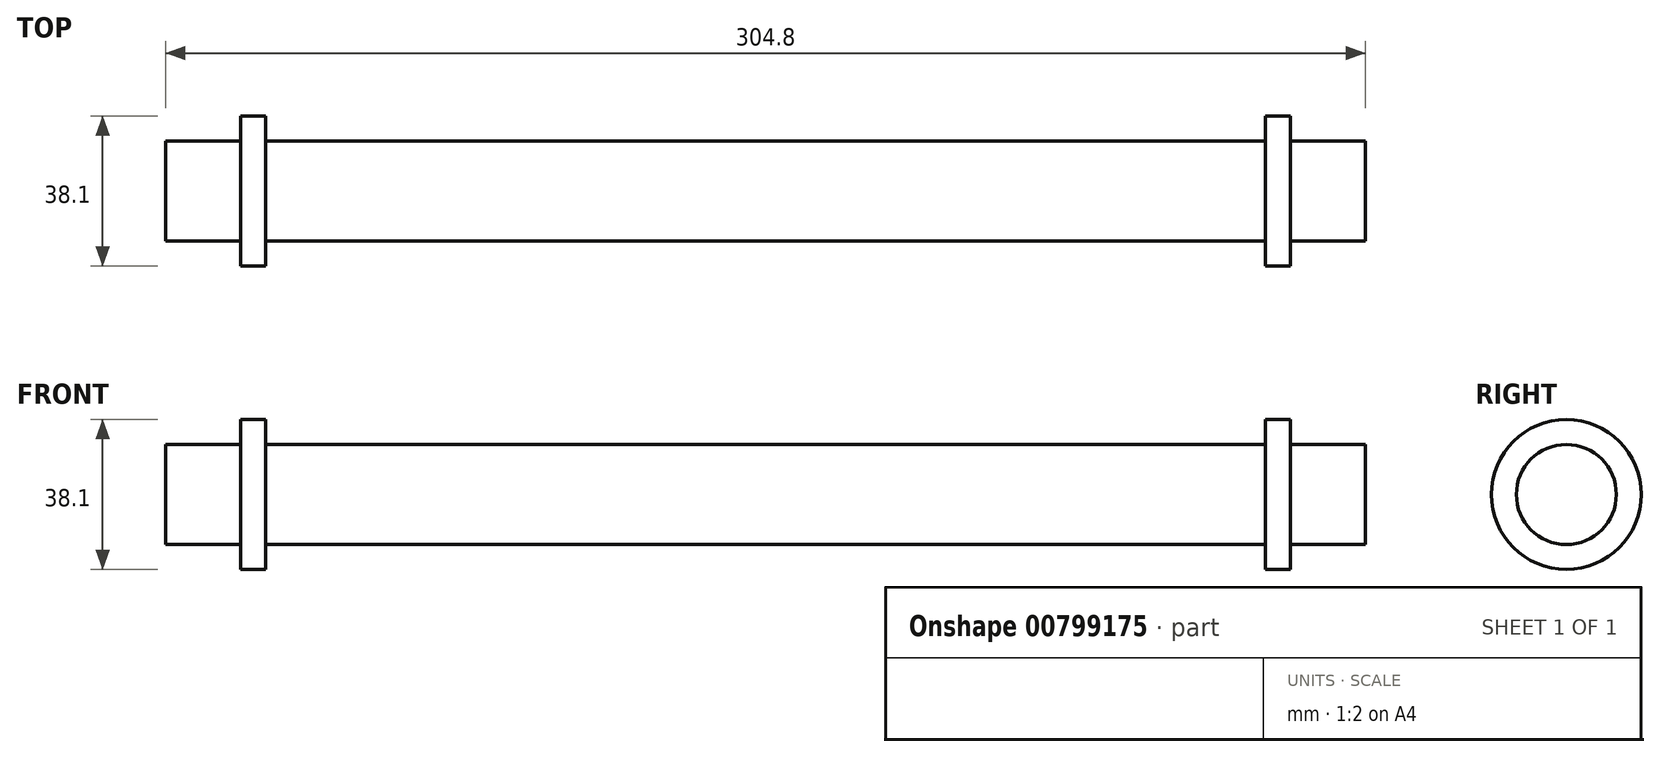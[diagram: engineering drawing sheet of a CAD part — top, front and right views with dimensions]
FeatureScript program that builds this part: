
annotation { "Feature Type Name" : "Feature", "Feature Type Description" : "" }
export const myFeature = defineFeature(function(context is Context, id is Id, definition is map)
    precondition{}
    {
        {
            var Q0;
            Q0=qCreatedBy(makeId("Right.planeOp"),FACE);
            var sketch = newSketch(context, id + "F0", { "sketchPlane" : qUnion([Q0])});
            skCircle(sketch, "E0", {"center": v(0, 0) * mm, "radius": 12.7 * mm});
            skSolve(sketch);
        }
        {
            var Q0;
            Q0=qSketchRegion(id+"F0",true);
            extrude(context, id + "F1", {"entities" : qUnion([Q0]), "endBound" : BoundingType.SYMMETRIC, "depth" : 304.8 * mm});
        }
        {
            var Q0;
            Q0=qCreatedBy(makeId("Front.planeOp"),FACE);
            var sketch = newSketch(context, id + "F2", { "sketchPlane" : qUnion([Q0])});
            skLineSegment(sketch, "E1.bottom", {"start": v(127, 12.7) * mm, "end": v(133.35, 12.7) * mm});
            skLineSegment(sketch, "E1.top", {"start": v(127, 19.05) * mm, "end": v(133.35, 19.05) * mm});
            skLineSegment(sketch, "E1.left", {"start": v(127, 12.7) * mm, "end": v(127, 19.05) * mm});
            skLineSegment(sketch, "E1.right", {"start": v(133.35, 12.7) * mm, "end": v(133.35, 19.05) * mm});
            skLineSegment(sketch, "E2.bottom", {"start": v(-133.35, 12.7) * mm, "end": v(-127, 12.7) * mm});
            skLineSegment(sketch, "E2.top", {"start": v(-133.35, 19.05) * mm, "end": v(-127, 19.05) * mm});
            skLineSegment(sketch, "E2.left", {"start": v(-133.35, 12.7) * mm, "end": v(-133.35, 19.05) * mm});
            skLineSegment(sketch, "E2.right", {"start": v(-127, 12.7) * mm, "end": v(-127, 19.05) * mm});
            skLineSegment(sketch, "E3", {"start": v(-152.4, 12.7) * mm, "end": v(-133.35, 12.7) * mm, "construction": true});
            skLineSegment(sketch, "E4", {"start": v(133.35, 12.7) * mm, "end": v(152.4, 12.7) * mm, "construction": true});
            skLineSegment(sketch, "E5", {"start": v(0, 0) * mm, "end": v(152.4, 0) * mm, "construction": true});
            skSolve(sketch);
        }
        {
            var Q0;
            Q0=makeQuery(id+"F2.imprint","IMPRINT",FACE,{"disambiguationData":[TD([[makeQuery(id+"F2.imprint","IMPRINT",EDGE,{"derivedFrom":sQuery(id+"F2.wireOp",EDGE,"E1.bottom")}),1.0]])]});
            var Q1;
            Q1=makeQuery(id+"F2.imprint","IMPRINT",FACE,{"disambiguationData":[TD([[makeQuery(id+"F2.imprint","IMPRINT",EDGE,{"derivedFrom":sQuery(id+"F2.wireOp",EDGE,"E2.bottom")}),1.0]])]});
            var Q2;
            Q2=sQuery(id+"F2.wireOp",EDGE,"E5");
            revolve(context, id + "F3", {"operationType" : NewBodyOperationType.ADD, "entities" : qUnion([Q0, Q1]), "axis" : qUnion([Q2]), "revolveType" : RevolveType.FULL});
        }
    });
